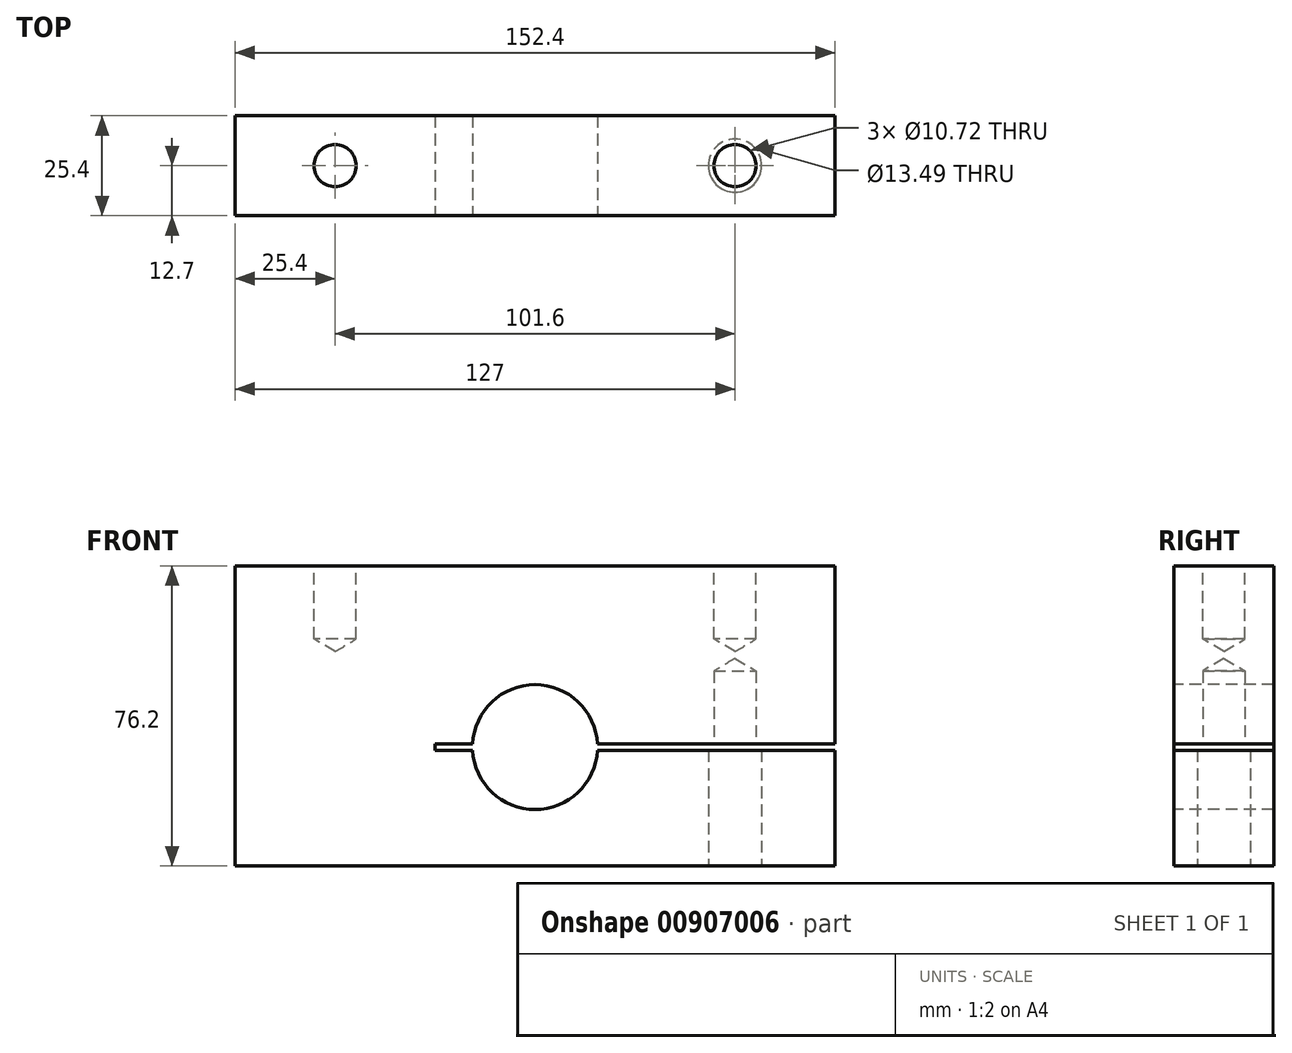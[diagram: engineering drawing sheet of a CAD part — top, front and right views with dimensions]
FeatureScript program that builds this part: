
annotation { "Feature Type Name" : "Feature", "Feature Type Description" : "" }
export const myFeature = defineFeature(function(context is Context, id is Id, definition is map)
    precondition{}
    {
        {
            var Q0;
            Q0=qCreatedBy(makeId("Front.planeOp"),FACE);
            var sketch = newSketch(context, id + "F0", { "sketchPlane" : qUnion([Q0])});
            skLineSegment(sketch, "E0.bottom", {"start": v(76.2, 33.6) * mm, "end": v(-76.2, 33.6) * mm});
            skLineSegment(sketch, "E0.top", {"start": v(76.2, -42.6) * mm, "end": v(-76.2, -42.6) * mm});
            skLineSegment(sketch, "E0.left", {"start": v(76.2, 33.6) * mm, "end": v(76.2, -42.6) * mm});
            skLineSegment(sketch, "E0.right", {"start": v(-76.2, 33.6) * mm, "end": v(-76.2, -42.6) * mm});
            skPoint(sketch, "E0.middle", {"position": v(0, -4.5) * mm});
            skSolve(sketch);
        }
        {
            var Q0;
            Q0=makeQuery(id+"F0.imprint","IMPRINT",FACE,{"disambiguationData":[TD([[makeQuery(id+"F0.imprint","IMPRINT",EDGE,{"derivedFrom":sQuery(id+"F0.wireOp",EDGE,"E0.bottom")}),1.0]])]});
            extrude(context, id + "F1", {"entities" : qUnion([Q0]), "depth" : 25.4 * mm, "offsetDistance" : 25.4 * mm, "symmetric" : true});
        }
        {
            var Q0;
            Q0=makeQuery(id+"F1.opExtrude","SWEPT_FACE",FACE,{"disambiguationData":[OSD([sQuery(id+"F0.wireOp",EDGE,"E0.bottom")])]});
            var sketch = newSketch(context, id + "F2", { "sketchPlane" : qUnion([Q0])});
            skLineSegment(sketch, "E1", {"start": v(-50.8, 0) * mm, "end": v(50.8, 0) * mm, "construction": true});
            skSolve(sketch);
        }
        {
            var Q0;
            Q0=sQuery(id+"F2.wireOp",VERTEX,"E1.start");
            var Q1;
            Q1=sQuery(id+"F2.wireOp",VERTEX,"E1.end");
            var Q2;
            Q2=makeQuery(id+"F1.opExtrude","SWEPT_BODY",BODY,{"disambiguationData":[OSD([sQuery(id+"F0.wireOp",EDGE,"E0.bottom"),sQuery(id+"F0.wireOp",EDGE,"E0.top"),sQuery(id+"F0.wireOp",EDGE,"E0.left"),sQuery(id+"F0.wireOp",EDGE,"E0.right")])]});
            hole(context, id + "F3", {"style" : HoleStyle.SIMPLE, "endStyle" : HoleEndStyle.BLIND, "standardTappedOrClearance" : lookupTablePath({ "standard" : "ANSI", "engagement" : "75%", "pitch" : "13 tpi", "size" : "1/2", "type" : "Tapped" }), "standardBlindInLast" : lookupTablePath({ "standard" : "ANSI", "fit" : "Free", "engagement" : "75%", "pitch" : "13 tpi", "size" : "1/2", "type" : "Clearance & tapped" }), "holeDiameter" : 10.72 * mm, "majorDiameter" : 12.7 * mm, "showTappedDepth" : true, "holeDepth" : 18.56 * mm, "isTappedThrough" : true, "tappedDepth" : 12.7 * mm, "tapClearance" : 3, "locations" : qUnion([Q0, Q1]), "scope" : qUnion([Q2])});
        }
        {
            var Q0;
            Q0=makeQuery(id+"F1.opExtrude","CAP_FACE",FACE,{"disambiguationData":[OSD([sQuery(id+"F0.wireOp",EDGE,"E0.bottom"),sQuery(id+"F0.wireOp",EDGE,"E0.top"),sQuery(id+"F0.wireOp",EDGE,"E0.left"),sQuery(id+"F0.wireOp",EDGE,"E0.right")])],"isStart":false});
            var sketch = newSketch(context, id + "F4", { "sketchPlane" : qUnion([Q0])});
            skLineSegment(sketch, "E2", {"start": v(0, 33.6) * mm, "end": v(0, -12.43) * mm, "construction": true});
            skCircle(sketch, "E3", {"center": v(0, -12.43) * mm, "radius": 15.88 * mm});
            skSolve(sketch);
        }
        {
            var Q0;
            Q0=makeQuery(id+"F4.imprint","IMPRINT",FACE,{"disambiguationData":[TD([[makeQuery(id+"F4.imprint","IMPRINT",EDGE,{"derivedFrom":sQuery(id+"F4.wireOp",EDGE,"E3")}),1.0]])]});
            extrude(context, id + "F5", {"entities" : qUnion([Q0]), "operationType" : NewBodyOperationType.REMOVE, "endBound" : BoundingType.THROUGH_ALL, "oppositeDirection" : true, "depth" : 25.4 * mm, "offsetDistance" : 25.4 * mm});
        }
        {
            var Q0;
            Q0=makeQuery(id+"F1.opExtrude","CAP_FACE",FACE,{"disambiguationData":[OSD([sQuery(id+"F0.wireOp",EDGE,"E0.bottom"),sQuery(id+"F0.wireOp",EDGE,"E0.top"),sQuery(id+"F0.wireOp",EDGE,"E0.left"),sQuery(id+"F0.wireOp",EDGE,"E0.right")])],"isStart":false});
            var sketch = newSketch(context, id + "F6", { "sketchPlane" : qUnion([Q0])});
            skCircle(sketch, "E4.0", {"center": v(0, -12.43) * mm, "radius": 15.88 * mm});
            skLineSegment(sketch, "E5.bottom", {"start": v(82.55, -11.64) * mm, "end": v(0, -11.64) * mm});
            skLineSegment(sketch, "E5.top", {"start": v(82.55, -13.22) * mm, "end": v(0, -13.22) * mm});
            skLineSegment(sketch, "E5.left", {"start": v(82.55, -11.64) * mm, "end": v(82.55, -13.22) * mm});
            skLineSegment(sketch, "E5.right", {"start": v(0, -11.64) * mm, "end": v(0, -13.22) * mm});
            skLineSegment(sketch, "E6", {"start": v(0, -11.64) * mm, "end": v(-25.4, -11.64) * mm});
            skLineSegment(sketch, "E7", {"start": v(-25.4, -11.64) * mm, "end": v(-25.4, -13.22) * mm});
            skLineSegment(sketch, "E8", {"start": v(-25.4, -13.22) * mm, "end": v(0, -13.22) * mm});
            skSolve(sketch);
        }
        {
            var Q0;
            {var subQ0=sQuery(id+"F6.wireOp",EDGE,"E5.left");Q0=makeQuery(id+"F6.imprint","IMPRINT",FACE,{"disambiguationData":[TD([[makeQuery(id+"F6.imprint","IMPRINT",EDGE,{"derivedFrom":subQ0}),-1.0]])]});}
            var Q1;
            {var subQ5=sQuery(id+"F6.wireOp",EDGE,"E5.right");Q1=makeQuery(id+"F6.imprint","IMPRINT",FACE,{"disambiguationData":[TD([[makeQuery(id+"F6.imprint","IMPRINT",EDGE,{"derivedFrom":subQ5}),1.0]])]});}
            var Q2;
            {var subQ0=sQuery(id+"F6.wireOp",EDGE,"E5.bottom");var subQ1=sQuery(id+"F6.wireOp",EDGE,"E4.0");var subQ2=makeQuery(id+"F6.imprint","INTERSECT",VERTEX,{"derivedFrom":[subQ1,subQ0]});Q2=makeQuery(id+"F6.imprint","IMPRINT",FACE,{"disambiguationData":[TD([[makeQuery(id+"F6.imprint","IMPRINT",EDGE,{"disambiguationData":[TD([[subQ2,1.0]])],"derivedFrom":subQ1}),-1.0]])]});}
            var Q3;
            {var subQ5=sQuery(id+"F6.wireOp",EDGE,"E5.right");Q3=makeQuery(id+"F6.imprint","IMPRINT",FACE,{"disambiguationData":[TD([[makeQuery(id+"F6.imprint","IMPRINT",EDGE,{"derivedFrom":subQ5}),-1.0]])]});}
            var Q4;
            {var subQ5=sQuery(id+"F6.wireOp",EDGE,"E7");Q4=makeQuery(id+"F6.imprint","IMPRINT",FACE,{"disambiguationData":[TD([[makeQuery(id+"F6.imprint","IMPRINT",EDGE,{"derivedFrom":subQ5}),1.0]])]});}
            extrude(context, id + "F7", {"entities" : qUnion([Q0, Q1, Q2, Q3, Q4]), "operationType" : NewBodyOperationType.REMOVE, "endBound" : BoundingType.THROUGH_ALL, "oppositeDirection" : true, "depth" : 25.4 * mm, "offsetDistance" : 25.4 * mm});
        }
        {
            var Q0;
            Q0=makeQuery(id+"F1.opExtrude","SWEPT_FACE",FACE,{"disambiguationData":[OSD([sQuery(id+"F0.wireOp",EDGE,"E0.top")])]});
            var sketch = newSketch(context, id + "F8", { "sketchPlane" : qUnion([Q0])});
            skLineSegment(sketch, "E9", {"start": v(0, 0) * mm, "end": v(50.8, 0) * mm, "construction": true});
            skCircle(sketch, "E10", {"center": v(50.8, 0) * mm, "radius": 6.74 * mm});
            skSolve(sketch);
        }
        {
            var Q0;
            Q0=makeQuery(id+"F8.imprint","IMPRINT",FACE,{"disambiguationData":[TD([[makeQuery(id+"F8.imprint","IMPRINT",EDGE,{"derivedFrom":sQuery(id+"F8.wireOp",EDGE,"E10")}),1.0]])]});
            extrude(context, id + "F9", {"entities" : qUnion([Q0]), "operationType" : NewBodyOperationType.REMOVE, "endBound" : BoundingType.UP_TO_NEXT, "oppositeDirection" : true, "depth" : 28.57 * mm, "offsetDistance" : 25.4 * mm});
        }
        {
            var Q0;
            Q0=makeQuery(id+"F7.boolean.opBoolean","COPY",FACE,{"derivedFrom":makeQuery(id+"F7.opExtrude","SWEPT_FACE",FACE,{"disambiguationData":[OSD([sQuery(id+"F6.wireOp",EDGE,"E5.bottom")])]})});
            var sketch = newSketch(context, id + "F10", { "sketchPlane" : qUnion([Q0])});
            skCircle(sketch, "E11.0", {"center": v(50.8, 0) * mm, "radius": 6.74 * mm});
            skSolve(sketch);
        }
        {
            var Q0;
            Q0=sQuery(id+"F10.wireOp",VERTEX,"E11.0.center");
            var Q1;
            Q1=makeQuery(id+"F1.opExtrude","SWEPT_BODY",BODY,{"disambiguationData":[OSD([sQuery(id+"F0.wireOp",EDGE,"E0.bottom"),sQuery(id+"F0.wireOp",EDGE,"E0.top"),sQuery(id+"F0.wireOp",EDGE,"E0.left"),sQuery(id+"F0.wireOp",EDGE,"E0.right")])]});
            hole(context, id + "F11", {"style" : HoleStyle.SIMPLE, "endStyle" : HoleEndStyle.BLIND, "standardTappedOrClearance" : lookupTablePath({ "standard" : "ANSI", "engagement" : "75%", "pitch" : "13 tpi", "size" : "1/2", "type" : "Tapped" }), "standardBlindInLast" : lookupTablePath({ "fit" : "Free", "standard" : "ANSI", "engagement" : "75%", "pitch" : "13 tpi", "size" : "1/2", "type" : "Clearance & tapped" }), "holeDiameter" : 10.72 * mm, "majorDiameter" : 12.7 * mm, "showTappedDepth" : true, "holeDepth" : 18.56 * mm, "isTappedThrough" : true, "tappedDepth" : 12.7 * mm, "tapClearance" : 3, "locations" : qUnion([Q0]), "scope" : qUnion([Q1])});
        }
    });
